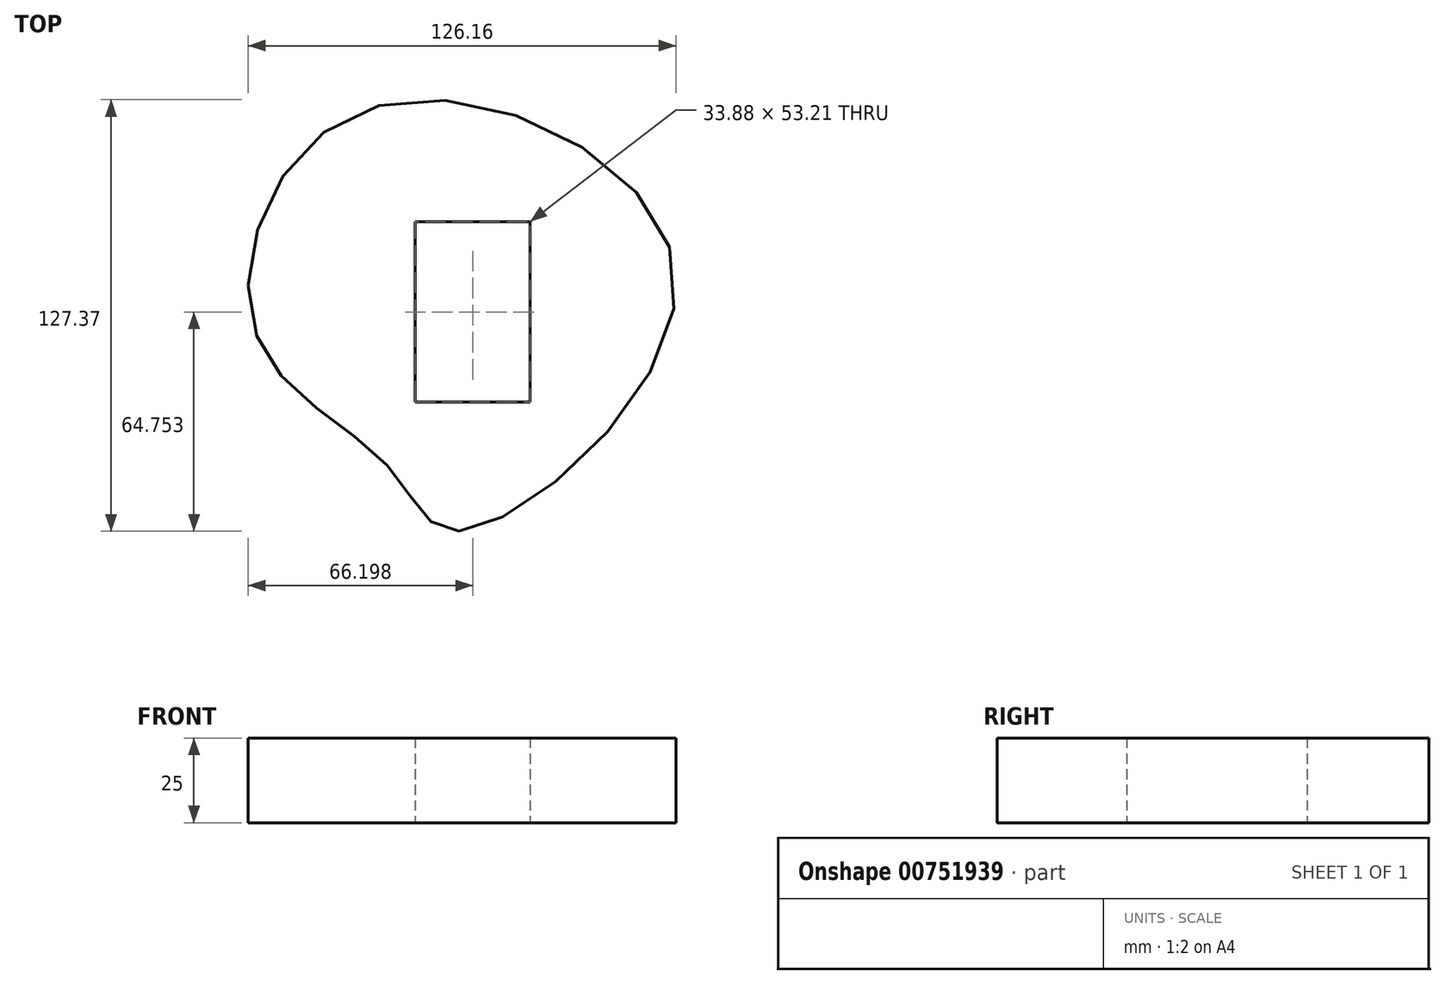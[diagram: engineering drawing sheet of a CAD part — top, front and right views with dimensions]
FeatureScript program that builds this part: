
annotation { "Feature Type Name" : "Feature", "Feature Type Description" : "" }
export const myFeature = defineFeature(function(context is Context, id is Id, definition is map)
    precondition{}
    {
        {
            var Q0;
            Q0=qCreatedBy(makeId("Top.planeOp"),FACE);
            var sketch = newSketch(context, id + "F0", { "sketchPlane" : qUnion([Q0])});
            skFitSpline(sketch, "E0", {"points": [v(-31.27, -38.13) * mm, v(-51.98, -19.2) * mm, v(-91.53, 20.77) * mm, v(-57.15, 86.95) * mm, v(32.54, 36.8) * mm, v(-31.27, -38.13) * mm]});
            skLineSegment(sketch, "E1.bottom", {"start": v(-44.26, 0) * mm, "end": v(-10.38, 0) * mm});
            skLineSegment(sketch, "E1.top", {"start": v(-44.26, 53.2) * mm, "end": v(-10.38, 53.2) * mm});
            skLineSegment(sketch, "E1.left", {"start": v(-44.26, 0) * mm, "end": v(-44.26, 53.2) * mm});
            skLineSegment(sketch, "E1.right", {"start": v(-10.38, 0) * mm, "end": v(-10.38, 53.2) * mm});
            skSolve(sketch);
        }
        {
            var Q0;
            Q0 = qSketchRegion(id + "F0", true);
            extrude(context, id + "F1", {"entities" : qUnion([Q0]), "depth" : 25 * mm, "offsetDistance" : 25 * mm});
        }
    });
